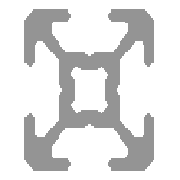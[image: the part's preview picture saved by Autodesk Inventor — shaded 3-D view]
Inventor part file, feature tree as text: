
AUTODESK INVENTOR PART (.ipt)
format: ipt  version: 2015 (Build 190159000, 159)  size: 377,344 bytes
history: native  units: mm
features: other x3, extrude x1, sketch x1
ambient origin geometry x8: Origin, YZ Plane, XZ Plane, XY Plane, X Axis, Y Axis, Z Axis, Center Point
bodies: Body1 (feature_tree)
feature tree (5):
  other  "Blocks"
  extrude  "Extrusion3"  [1 undecoded]
  sketch  "Sketch1"  dims[d23=0.0mm]
  other  "20x20"
  other  "20x20:1"
note: 1 required parameter value undecoded (feature->parameter linkage not recoverable at this tier; creation-order binding heuristic only, values carry confidence <= 0.55)
